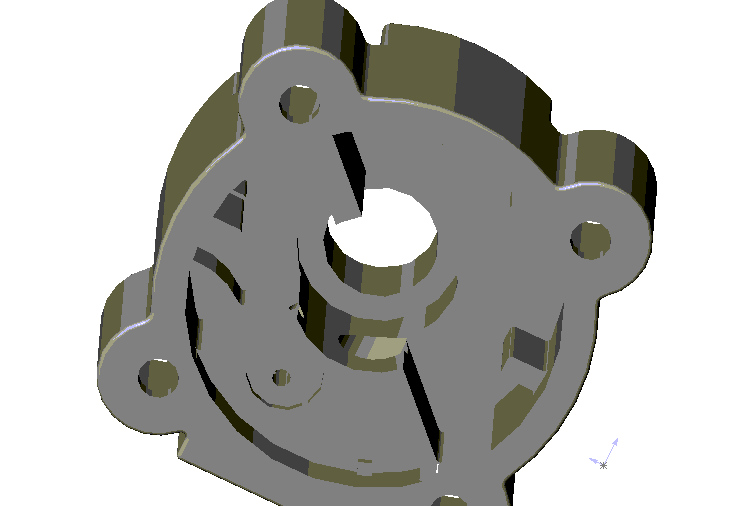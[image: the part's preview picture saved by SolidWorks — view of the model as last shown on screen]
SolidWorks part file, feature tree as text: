
SOLIDWORKS PART (.sldprt)
format: sldprt  version: not decoded by parser v0  size: 1,054,208 bytes
history: native  units: mm
features: fillet x24, sketch x23, cut_extrude x12, hole x4, plane x3, extrude x3, chamfer x1 + 1 further entry (+6 scaffold rows collapsed)
feature tree (77):
  scaffold x6  (default folders/planes/origin — collapsed)
  "Corps de surface"
  plane  "Plan1"
  plane  "Plan2"
  plane  "Plan3"
  sketch  "Esquisse1"
  extrude  "Base-Extrusion"  Depth=50mm
  sketch  "Esquisse2"  dims[D1=45.0mm D4=17.0mm D5=17.0mm D6=17.0mm D7=17.0mm D2=50.0mm D3=50.0mm D8=15.0mm D9=15.0mm D10=15.0mm D11=15.0mm D12=15.0mm D13=15.0mm D14=15.0mm D15=15.0mm]
  cut_extrude  "Enlèv. mat.-Extru.5"  Depth=46mm
  sketch  "Esquisse7"  dims[c1.D3=40.0mm c1.D4=40.0mm c1.D5=33.0mm c1.D1=35.0mm c1.D2=35.0mm c2.D3=50.0mm c2.D1=50.0mm c2.D2=50.0mm c3.D3=35.0mm c3.D4=35.0mm]
  cut_extrude  "Enlèv. mat.-Extru.9"  Depth=15mm
  sketch  "Esquisse11"  dims[D1=36.0mm D2=50.0mm D3=50.0mm]
  cut_extrude  "Enlèv. mat.-Extru.12"  Depth=44mm
  sketch  "Esquisse12"  dims[D1=27.0mm D2=27.0mm D3=27.0mm D4=27.0mm D5=97.0mm D6=1.0mm]
  cut_extrude  "Enlèv. mat.-Extru.13"  [1 undecoded]
  sketch  "Esquisse13"  dims[D1=9.0mm]
  cut_extrude  "Enlèv. mat.-Extru.14"  [1 undecoded]
  fillet  "Congé1"  Radius=2mm
  fillet  "Congé2"  Radius=2mm
  fillet  "Congé5"  Radius=2mm
  fillet  "Congé6"  Radius=2mm
  fillet  "Congé7"  Radius=2mm
  fillet  "Congé8"  Radius=2mm
  sketch  "Esquisse14"  dims[D1=45.0mm]
  extrude  "Boss.-Extru.1"  Depth=5mm
  fillet  "Congé9"  Radius=1mm
  fillet  "Congé10"  Radius=2mm
  fillet  "Congé11"  Radius=2mm
  fillet  "Congé12"  Radius=2mm
  fillet  "Congé15"  Radius=2mm
  fillet  "Congé16"  Radius=2mm
  fillet  "Congé17"  Radius=2mm
  fillet  "Congé18"  Radius=1mm
  fillet  "Congé19"  Radius=0.5mm
  fillet  "Congé20"  Radius=0.5mm
  fillet  "Congé21"  Radius=0.5mm
  fillet  "Congé22"  Radius=0.5mm
  sketch  "Esquisse15"  dims[c1.D1=92.0mm c1.D2=51.0mm c1.D3=44.0mm c1.D4=5.0mm c1.D5=5.0mm c2.D4=~25.495098mm]
  cut_extrude  "Enlèv. mat.-Extru.15"  Depth=2mm
  fillet  "Congé23"  Radius=1mm
  fillet  "Congé25"  Radius=0.5mm
  fillet  "Congé28"  Radius=0.5mm
  fillet  "Congé32"  Radius=1mm
  sketch  "Esquisse18"  dims[c1.D1=82.0mm c1.D2=15.0mm c1.D3=~12.454202mm c2.D3=~4.980751deg c3.D3=3.0mm c3.D4=3.0mm]
  sketch  "Esquisse19"  dims[D1=82.0mm]
  cut_extrude  "Enlèv. mat.-Extru.18"  Depth=8mm
  cut_extrude  "Enlèv. mat.-Extru.19"  Depth=10mm
  sketch  "Esquisse20"  dims[c1.D1=82.0mm c1.D8=1.0mm c1.D9=0.5mm c1.D10=1.0mm c1.D2=2.0mm c1.D3=4.0mm c1.D4=3.0mm c1.D5=5.0mm c1.D6=32.0mm c1.D7=23.0mm c2.D8=~9.369165mm c3.D8=45.0deg]
  cut_extrude  "Enlèv. mat.-Extru.20"  Depth=20mm
  sketch  "Esquisse21"  dims[c1.D1=1.0mm c1.D2=1.0mm c1.D3=36.0mm c1.D4=36.0mm c1.D5=36.0mm c1.D6=1.0mm c1.D7=41.0mm c2.D1=82.0mm c2.D2=1.0mm c2.D7=1.0mm c2.D8=1.0mm]
  cut_extrude  "Enlèv. mat.-Extru.22"  Depth=10mm
  hole  "Perçage1"  Diameter=15mm Depth=33.279788mm
  sketch  "Esquisse24"  dims[D1=26.0mm D2=16.0mm]
  sketch  "Esquisse23"  dims[Diamètre=15.0mm Profondeur=~33.279788mm]
  hole  "Perçage2"  Diameter=4mm Depth=36.89006mm
  sketch  "Esquisse26"  dims[D1=19.0mm D2=35.0mm]
  sketch  "Esquisse25"  dims[Diamètre=4.0mm Profondeur=~36.89006mm]
  hole  "Perçage3"  Diameter=17mm Depth=2mm
  sketch  "Esquisse28"  dims[c1.D1=~25.600723mm c1.D2=24.0mm c1.D3=13.0mm c2.D1=13.0mm]
  sketch  "Esquisse27"  dims[Diamètre=17.0mm Profondeur=2.0mm]
  hole  "Perçage4"  Diameter=4mm Depth=15mm
  sketch  "Esquisse30"  dims[c1.D1=13.0mm c1.D2=22.0mm c2.D1=13.0mm]
  sketch  "Esquisse29"  dims[Diamètre=4.0mm Profondeur=15.0mm]
  sketch  "Esquisse31"  dims[D1=42.0mm]
  extrude  "Boss.-Extru.2"  Depth=23mm
  sketch  "Esquisse32"  dims[c1.D1=35.0mm c1.D2=4.0mm c1.D3=~21.594138mm c1.D4=8.0mm c1.D5=0.001mm c2.D3=2.0mm]
  cut_extrude  "Enlèv. mat.-Extru.23"  Depth=15mm
  sketch  "Esquisse33"  dims[D1=25.0mm]
  cut_extrude  "Enlèv. mat.-Extru.24"  [1 undecoded]
  chamfer  "Chanfrein1"  Distance=0.5mm Angle=45deg
  fillet  "Congé33"  Radius=1mm
  fillet  "Congé34"  Radius=1mm
decode coverage: 63 of 67 modeling features carry decoded parameters; 1 rows unclassified (native names shown)
note: ~ marks probable driven/reference dimensions
note: 3 parameter values undecoded
summary: no parameter record found for 3 features; Diameter pulled from absorbed wizard sketch
note: suppression state not decoded; provenance and decode notes live in map.json
